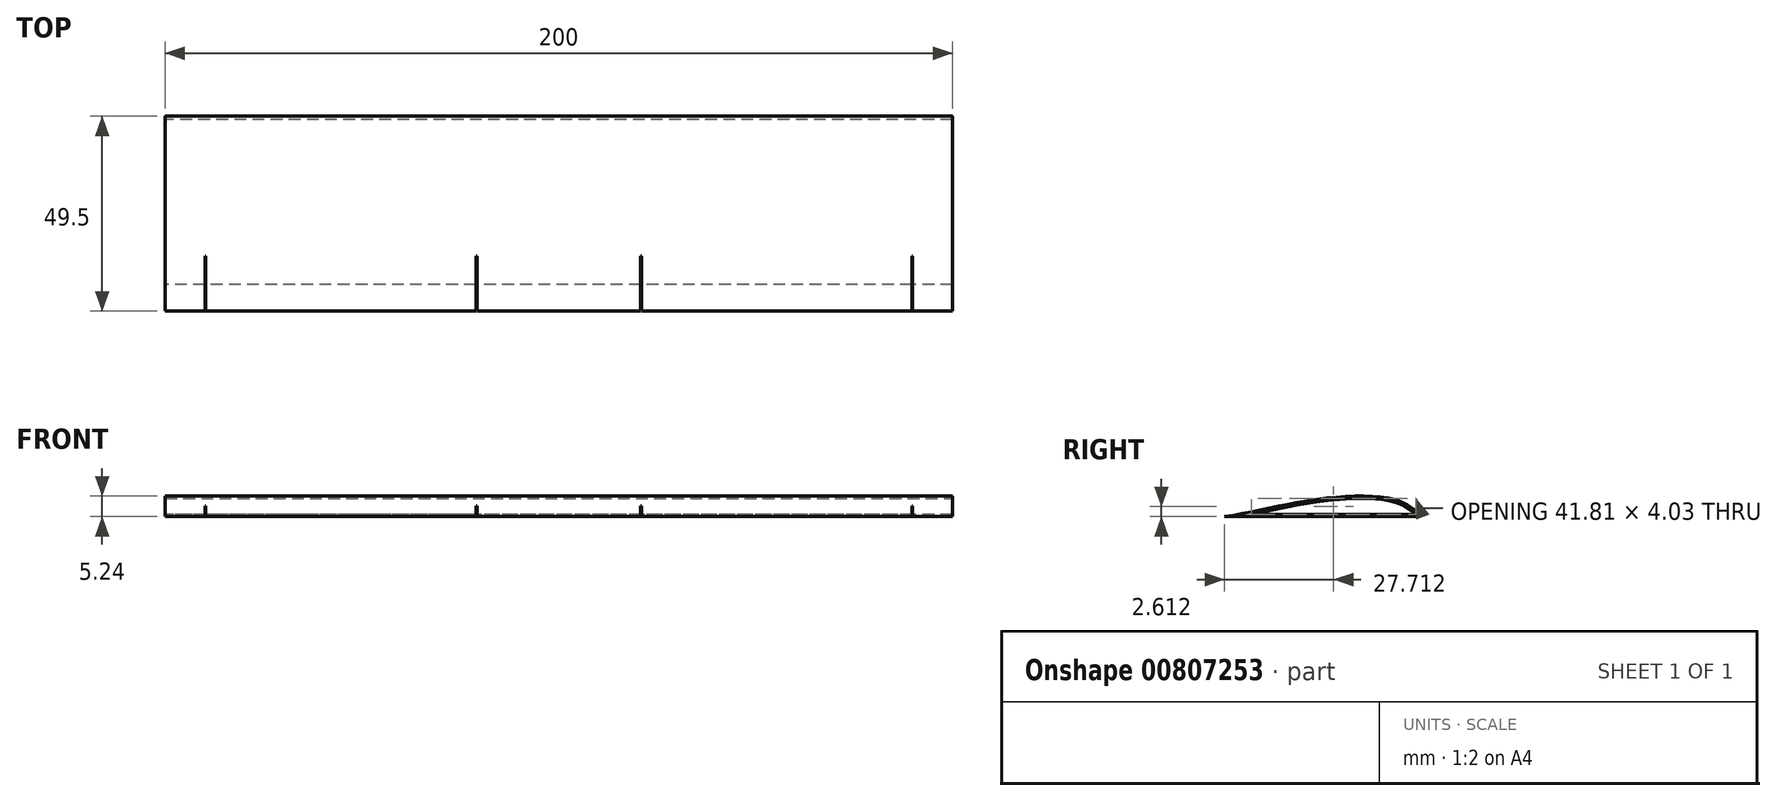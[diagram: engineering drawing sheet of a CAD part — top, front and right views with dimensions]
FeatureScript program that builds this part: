
annotation { "Feature Type Name" : "Feature", "Feature Type Description" : "" }
export const myFeature = defineFeature(function(context is Context, id is Id, definition is map)
    precondition{}
    {
        {
            var Q0;
            Q0=qCreatedBy(makeId("Right.planeOp"),FACE);
            var sketch = newSketch(context, id + "F0", { "sketchPlane" : qUnion([Q0])});
            skLineSegment(sketch, "E0", {"start": v(-31.55, -3.85) * mm, "end": v(18.45, -3.85) * mm});
            skFitSpline(sketch, "E1", {"points": [v(18.45, -3.85) * mm, v(8.1, 1.15) * mm, v(-11.69, 0) * mm, v(-31.55, -3.85) * mm], "startDerivative": vector(-31.54, 36.77) * mm, "endDerivative": vector(-54.22, -7.78) * mm});
            skSolve(sketch);
        }
        {
            var Q0;
            Q0 = qSketchRegion(id + "F0", true);
            extrude(context, id + "F1", {"entities" : qUnion([Q0]), "depth" : 200 * mm, "offsetDistance" : 25 * mm});
        }
        {
            var Q0;
            Q0=makeQuery(id+"F1.opExtrude","SWEPT_BODY",BODY,{"disambiguationData":[OSD([sQuery(id+"F0.wireOp",EDGE,"E0"),sQuery(id+"F0.wireOp",EDGE,"E1")])]});
            transform(context, id + "F2", {"entities" : qUnion([Q0]), "transformType" : TransformType.TRANSLATION_3D, "dx" : -100 * mm, "dy" : 0 * mm, "dz" : 16.3 * mm, "makeCopy" : false});
        }
        {
            var Q0;
            Q0=makeQuery(id+"F1.opExtrude","SWEPT_FACE",FACE,{"disambiguationData":[OSD([sQuery(id+"F0.wireOp",EDGE,"E0")])]});
            var sketch = newSketch(context, id + "F3", { "sketchPlane" : qUnion([Q0])});
            skLineSegment(sketch, "E2.bottom", {"start": v(89.9, 17.55) * mm, "end": v(89.7, 17.55) * mm});
            skLineSegment(sketch, "E2.top", {"start": v(89.9, 31.55) * mm, "end": v(89.7, 31.55) * mm});
            skLineSegment(sketch, "E2.left", {"start": v(89.9, 17.55) * mm, "end": v(89.9, 31.55) * mm});
            skLineSegment(sketch, "E2.right", {"start": v(89.7, 17.55) * mm, "end": v(89.7, 31.55) * mm});
            skLineSegment(sketch, "E3.MirrorCS", {"start": v(-89.7, 17.55) * mm, "end": v(-89.7, 31.55) * mm});
            skLineSegment(sketch, "E4.MirrorCS", {"start": v(-89.9, 17.55) * mm, "end": v(-89.9, 31.55) * mm});
            skLineSegment(sketch, "E5.MirrorCS", {"start": v(-89.9, 17.55) * mm, "end": v(-89.7, 17.55) * mm});
            skLineSegment(sketch, "E6.MirrorCS", {"start": v(-89.9, 31.55) * mm, "end": v(-89.7, 31.55) * mm});
            skSolve(sketch);
        }
        {
            var Q0;
            Q0=makeQuery(id+"F1.opExtrude","CAP_FACE",FACE,{"disambiguationData":[OSD([sQuery(id+"F0.wireOp",EDGE,"E0"),sQuery(id+"F0.wireOp",EDGE,"E1")])],"isStart":false});
            var Q1;
            Q1=makeQuery(id+"F1.opExtrude","CAP_FACE",FACE,{"disambiguationData":[OSD([sQuery(id+"F0.wireOp",EDGE,"E0"),sQuery(id+"F0.wireOp",EDGE,"E1")])],"isStart":true});
            shell(context, id + "F4", {"entities" : qUnion([Q0, Q1]), "thickness" : 0.6 * mm});
        }
        {
            var Q0;
            Q0=makeQuery(id+"F3.imprint","IMPRINT",FACE,{"disambiguationData":[TD([[makeQuery(id+"F3.imprint","IMPRINT",EDGE,{"derivedFrom":sQuery(id+"F3.wireOp",EDGE,"E2.bottom")}),-1.0]])]});
            var Q1;
            Q1=makeQuery(id+"F3.imprint","IMPRINT",FACE,{"disambiguationData":[TD([[makeQuery(id+"F3.imprint","IMPRINT",EDGE,{"derivedFrom":sQuery(id+"F3.wireOp",EDGE,"E3.MirrorCS")}),1.0]])]});
            extrude(context, id + "F5", {"entities" : qUnion([Q0, Q1]), "operationType" : NewBodyOperationType.REMOVE, "oppositeDirection" : true, "depth" : 25 * mm, "offsetDistance" : 25 * mm});
        }
        {
            var Q0;
            Q0=makeQuery(id+"F1.opExtrude","SWEPT_FACE",FACE,{"disambiguationData":[OSD([sQuery(id+"F0.wireOp",EDGE,"E0")])]});
            var sketch = newSketch(context, id + "F6", { "sketchPlane" : qUnion([Q0])});
            skLineSegment(sketch, "E7.bottom", {"start": v(-21, 31.55) * mm, "end": v(-20.8, 31.55) * mm});
            skLineSegment(sketch, "E7.top", {"start": v(-21, 17.55) * mm, "end": v(-20.8, 17.55) * mm});
            skLineSegment(sketch, "E7.left", {"start": v(-21, 31.55) * mm, "end": v(-21, 17.55) * mm});
            skLineSegment(sketch, "E7.right", {"start": v(-20.8, 31.55) * mm, "end": v(-20.8, 17.55) * mm});
            skLineSegment(sketch, "E8.MirrorCS", {"start": v(20.8, 31.55) * mm, "end": v(20.8, 17.55) * mm});
            skLineSegment(sketch, "E9.MirrorCS", {"start": v(21, 31.55) * mm, "end": v(21, 17.55) * mm});
            skLineSegment(sketch, "E10.MirrorCS", {"start": v(21, 17.55) * mm, "end": v(20.8, 17.55) * mm});
            skLineSegment(sketch, "E11.MirrorCS", {"start": v(21, 31.55) * mm, "end": v(20.8, 31.55) * mm});
            skSolve(sketch);
        }
        {
            var Q0;
            Q0 = qSketchRegion(id + "F6", true);
            extrude(context, id + "F7", {"entities" : qUnion([Q0]), "operationType" : NewBodyOperationType.REMOVE, "oppositeDirection" : true, "depth" : 25 * mm, "offsetDistance" : 25 * mm});
        }
        {
            var Q0;
            {var subQ0=sQuery(id+"F0.wireOp",EDGE,"E1");var subQ1=sQuery(id+"F0.wireOp",EDGE,"E0");Q0=makeQuery(id+"F1.opExtrude","SWEPT_EDGE",EDGE,{"disambiguationData":[OSD([subQ1,subQ0]),TDD([makeQuery(id+"F0.imprint","INTERSECT",VERTEX,{"disambiguationData":[OD(1.0)],"derivedFrom":[subQ1,subQ0]})])]});}
            fillet(context, id + "F8", {"entities" : qUnion([Q0]), "radius" : 0.4 * mm, "tangentPropagation" : true, "allowEdgeOverflow" : false});
        }
    });
